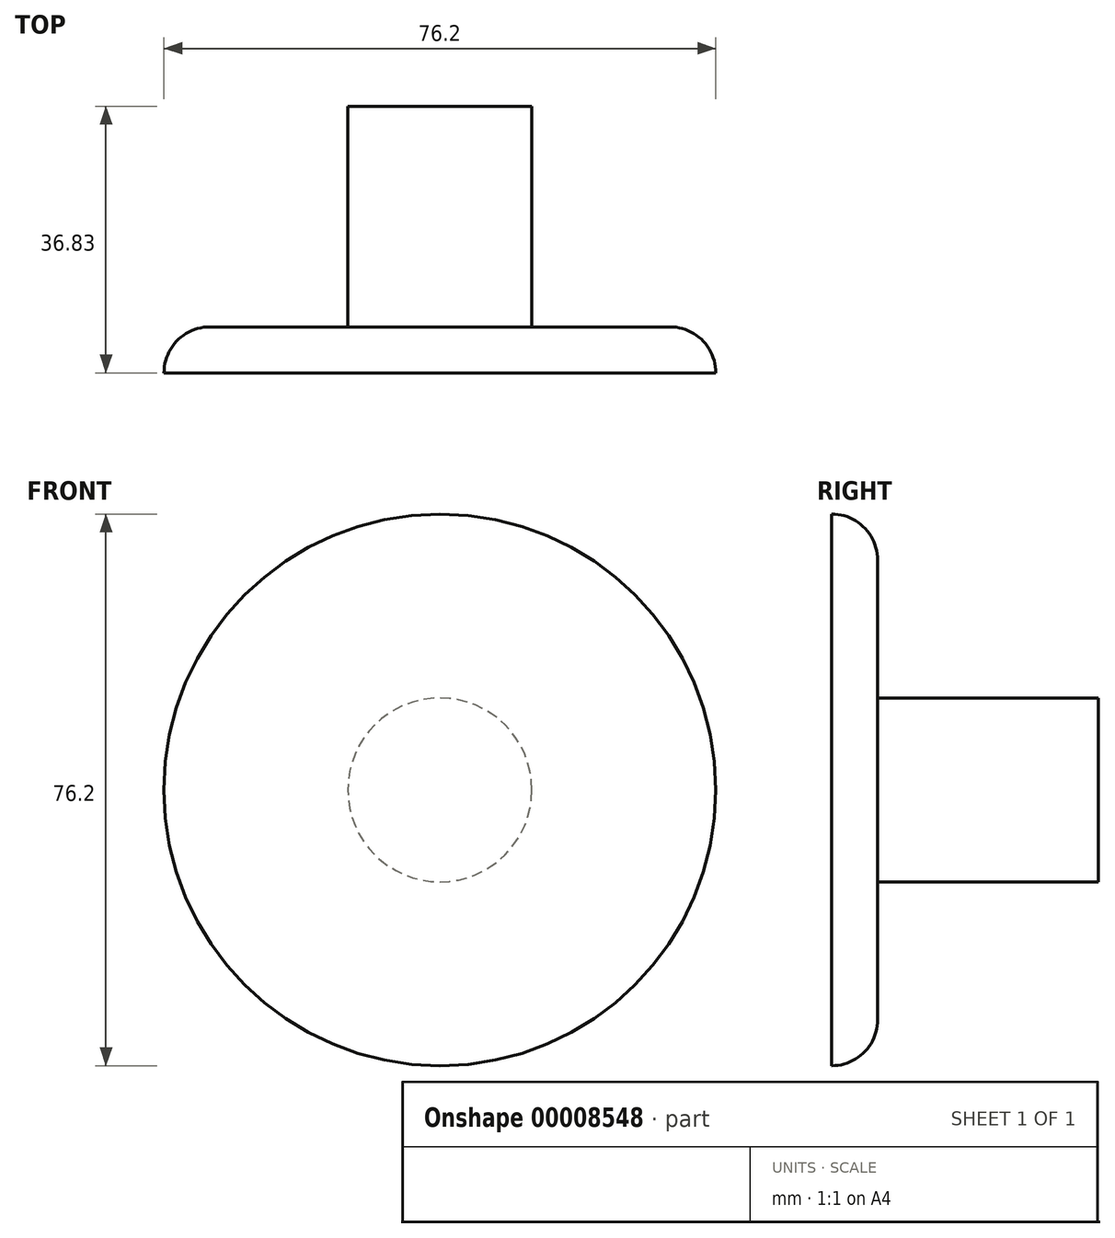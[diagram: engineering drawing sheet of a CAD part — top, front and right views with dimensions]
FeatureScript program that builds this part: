
annotation { "Feature Type Name" : "Feature", "Feature Type Description" : "" }
export const myFeature = defineFeature(function(context is Context, id is Id, definition is map)
    precondition{}
    {
        {
            var Q0;
            Q0=qCreatedBy(makeId("Front.planeOp"),FACE);
            var sketch = newSketch(context, id + "F0", { "sketchPlane" : qUnion([Q0])});
            skCircle(sketch, "E0", {"center": v(0, 0) * mm, "radius": 12.7 * mm});
            skSolve(sketch);
        }
        {
            var Q0;
            Q0=makeQuery(id+"F0.imprint","IMPRINT",FACE,{"disambiguationData":[TD([[makeQuery(id+"F0.imprint","IMPRINT",EDGE,{"derivedFrom":sQuery(id+"F0.wireOp",EDGE,"E0")}),1.0]])]});
            extrude(context, id + "F1", {"entities" : qUnion([Q0]), "depth" : 30.48 * mm});
        }
        {
            var Q0;
            Q0=makeQuery(id+"F1.opExtrude","CAP_FACE",FACE,{"disambiguationData":[OSD([sQuery(id+"F0.wireOp",EDGE,"E0")])],"isStart":false});
            var sketch = newSketch(context, id + "F2", { "sketchPlane" : qUnion([Q0])});
            skCircle(sketch, "E1", {"center": v(0, 0) * mm, "radius": 38.1 * mm});
            skSolve(sketch);
        }
        {
            var Q0;
            Q0=makeQuery(id+"F2.imprint","IMPRINT",FACE,{"disambiguationData":[TD([[makeQuery(id+"F2.imprint","IMPRINT",EDGE,{"derivedFrom":sQuery(id+"F2.wireOp",EDGE,"E1")}),1.0]])]});
            var Q1;
            Q1=makeQuery(id+"F2.imprint","IMPRINT",FACE,{"disambiguationData":[TD([[makeQuery(id+"F2.imprint","IMPRINT",EDGE,{"derivedFrom":makeQuery(id+"F1.opExtrude","CAP_EDGE",EDGE,{"disambiguationData":[OSD([sQuery(id+"F0.wireOp",EDGE,"E0")])],"isStart":false})}),1.0]])]});
            extrude(context, id + "F3", {"entities" : qUnion([Q0, Q1]), "operationType" : NewBodyOperationType.ADD, "depth" : 6.35 * mm});
        }
        {
            var Q0;
            Q0=makeQuery(id+"F1.opExtrude","CAP_EDGE",EDGE,{"disambiguationData":[OSD([sQuery(id+"F0.wireOp",EDGE,"E0")])],"isStart":false});
            var Q1;
            Q1=makeQuery(id+"F3.opExtrude","CAP_EDGE",EDGE,{"disambiguationData":[OSD([sQuery(id+"F2.wireOp",EDGE,"E1")])],"isStart":true});
            fillet(context, id + "F4", {"entities" : qUnion([Q0, Q1]), "radius" : 6.35 * mm, "tangentPropagation" : true, "allowEdgeOverflow" : false});
        }
    });
